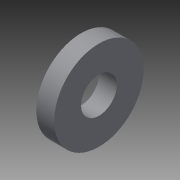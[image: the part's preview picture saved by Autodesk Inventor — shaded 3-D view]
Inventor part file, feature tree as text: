
AUTODESK INVENTOR PART (.ipt)
format: ipt  version: 2013 (Build 170138000, 138)  size: 75,776 bytes
history: native  units: mm
features: other x1, extrude x1, sketch x1
ambient origin geometry x8: Origin, YZ Plane, XZ Plane, XY Plane, X Axis, Y Axis, Z Axis, Center Point
feature tree (3):
  other  "ソリッド1"
  extrude  "押し出し1"  Depth=2.0mm
  sketch  "スケッチ1"
